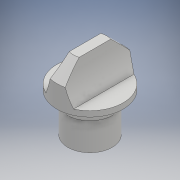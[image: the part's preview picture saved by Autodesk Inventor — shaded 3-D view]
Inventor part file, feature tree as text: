
AUTODESK INVENTOR PART (.ipt)
format: ipt  version: 2017 (Build 210142000, 142)  size: 300,544 bytes
history: native  units: mm
features: extrude x5, sketch x5, chamfer x2, projected_geometry x2, hole x1, plane x1, reference x1
ambient origin geometry x8: Origin, YZ Plane, XZ Plane, XY Plane, X Axis, Y Axis, Z Axis, Center Point
bodies: Solid1 (feature_tree)
feature tree (17):
  extrude  "Extrusion1"  Depth=1.0mm TaperAngle=0.0deg
  extrude  "Extrusion2"  Depth=6.0mm TaperAngle=0.0deg
  extrude  "Extrusion3"  Depth=1.0mm TaperAngle=0.0deg
  hole  "Hole1"  [1 undecoded]
  extrude  "Extrusion4"  Depth=15.0mm
  plane  "Work Plane1"
  extrude  "Extrusion5"  Depth=15.0mm TaperAngle=0.0deg
  chamfer  "Chamfer1"  Distance=15.0mm
  chamfer  "Chamfer2"  Distance=15.0mm
  sketch  "Sketch1"  dims[d0=8.0mm d1=1.0mm d2=0.0mm]
  reference  "Reference1"
  sketch  "Sketch2"  dims[d3=8.0mm d4=6.0mm d5=0.0mm]
  sketch  "Sketch3"  dims[d6=12.0mm d7=1.0mm d8=0.0mm]
  sketch  "Sketch4"  dims[d18=10.0mm d19=10.0mm d11=3.9mm d12=6.0mm d13=4.0mm d14=2.0mm d15=90.0deg d16=8.0mm d17=20.594885mm d20=6.0mm d21=0.0mm]
  projected_geometry  "Projected Loop1"
  sketch  "Sketch5"  dims[d22=2.5mm d23=2.5mm d24=6.0mm d25=0.0mm d26=15.0mm d27=15.0mm d28=1.8mm d29=1.8mm d30=3.0mm d31=2.0mm d32=45.0deg d33=2.0mm d34=2.0mm d35=45.0deg]
  projected_geometry  "Projected Loop2"
note: 1 required parameter value undecoded (feature->parameter linkage not recoverable at this tier; creation-order binding heuristic only, values carry confidence <= 0.55)
